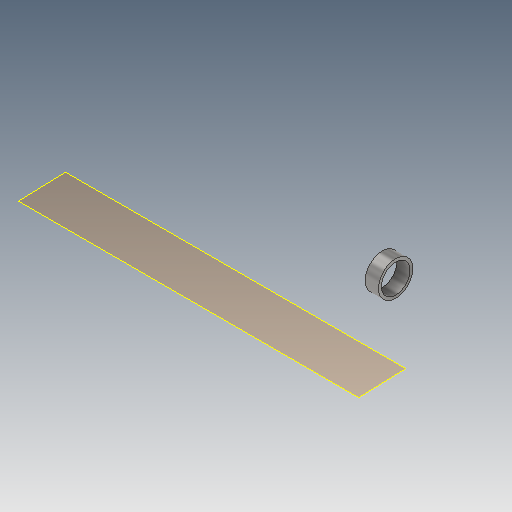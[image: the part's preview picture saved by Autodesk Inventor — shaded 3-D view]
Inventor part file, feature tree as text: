
AUTODESK INVENTOR PART (.ipt)
format: ipt  version: 2025 (Build 290162000, 162)  size: 96,768 bytes
history: native  units: mm
features: other x5, reference x3, plane x1, revolve x1, sketch x1
ambient origin geometry x8: Origin, YZ Plane, XZ Plane, XY Plane, X Axis, Y Axis, Z Axis, Center Point
bodies: 实体1 (feature_tree)
feature tree (11):
  plane  "工作平面1"
  revolve  "旋转1"  Angle=90.0deg
  sketch  "草图1"  dims[d0=18.0mm d1=90.0deg]
  reference  "参考1"
  reference  "参考2"
  reference  "参考3"
  other  "齿轮箱.iam"
  other  "高速轴:1"
  other  "轴承:1"
  other  "滚动轴承 GB/T 276-1994 60000 和 160000 型 6206:1"
  other  "轴:1"
